# Revit family: 0230DY-M54-XK
name_source: partatom
category: Plumbing Fixtures
revit_build: Autodesk Revit MEP 2012 (Build: 20110309_2315(x64)
units: mm (PartAtom-declared; Revit-internal decimal feet)

## types (1)
- 0250DY-M54-XK
    ATS URL = http://www.atsspec.net
    Assembly Code = D2010100
    CW Connection = Yes
    CWFU = 0
    Default Elevation = 0"
    Description = Adjustable fixture supports for siphon jet water closets - Shallow rough-in type. No-hub vertical fittings with two side inlets.
    HW Connection = No
    HWFU = 0
    Height = 18 1/4"
    Installation Type = Floor Mounted
    Length = 23 5/32"
    Manufacturer = Jay R. Smith
    Masterformat Number = 22 41 13 13
    Masterformat Title = Residential Water Closets
    Material = Metal-Jay R. Smith-Cast Iron
    Model = 0250DY-M54-XK
    Omniclass Table 23 Code = 23.45.05.21.11.11
    Omniclass Table 23 Title = Water Operated Water Closets
    Price = Prices may vary. Please consult Manufacturer Representative for most up-to-date price list.
    Product Documentation Link = http://www.jrsmith.com
    URL = http://www.jrsmith.com
    Vent Connection = No
    WFU = 0
    Waste Connection = Yes
    Waste Connection Diameter = 4"
    Waste Connection Radius = 2"
    Width = 16 1/2"
